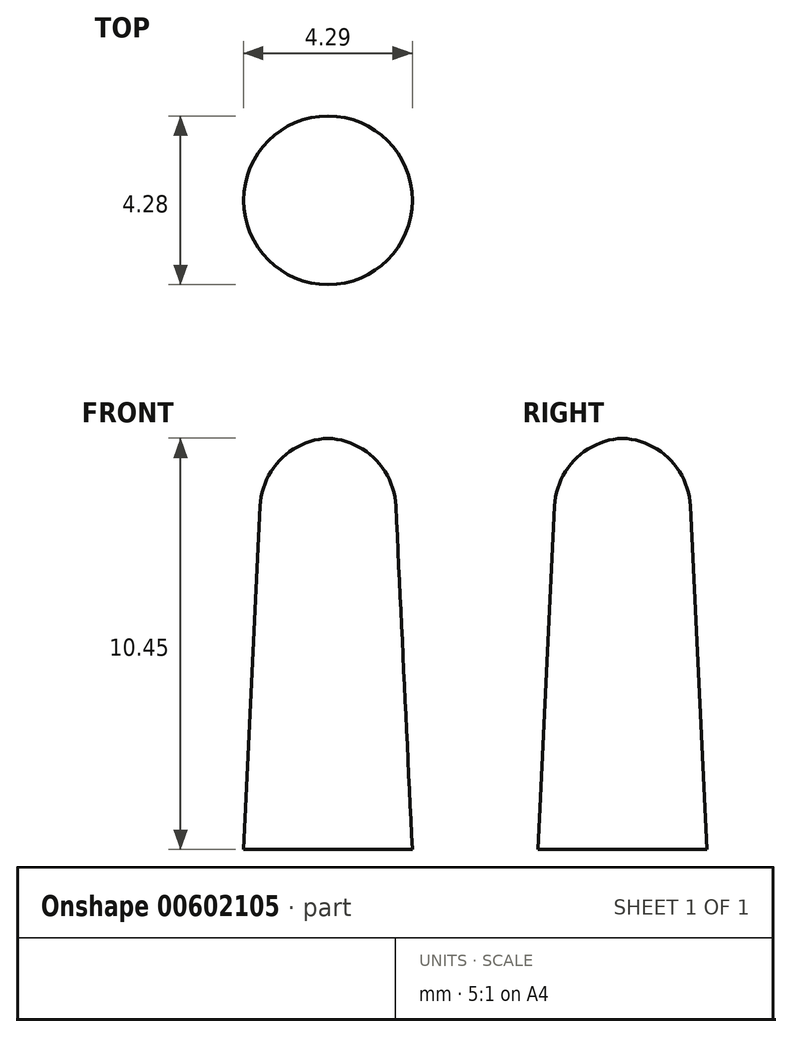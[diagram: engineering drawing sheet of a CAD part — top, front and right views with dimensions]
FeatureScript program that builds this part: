
annotation { "Feature Type Name" : "Feature", "Feature Type Description" : "" }
export const myFeature = defineFeature(function(context is Context, id is Id, definition is map)
    precondition{}
    {
        {
            var Q0;
            Q0=qCreatedBy(makeId("Front.planeOp"),FACE);
            var sketch = newSketch(context, id + "F0", { "sketchPlane" : qUnion([Q0])});
            skLineSegment(sketch, "E0", {"start": v(-32.4, 48.83) * mm, "end": v(-32.4, 38.38) * mm});
            skLineSegment(sketch, "E1", {"start": v(-32.4, 38.38) * mm, "end": v(-30.26, 38.38) * mm});
            skLineSegment(sketch, "E2", {"start": v(-30.68, 47.1) * mm, "end": v(-30.26, 38.38) * mm});
            skArc(sketch, "E3", {"start": v(-30.68, 47.1) * mm, "mid": v(-31.2, 48.3) * mm, "end": v(-32.4, 48.83) * mm});
            skSolve(sketch);
        }
        {
            var Q0;
            Q0=makeQuery(id+"F0.imprint","IMPRINT",FACE,{"disambiguationData":[TD([[makeQuery(id+"F0.imprint","IMPRINT",EDGE,{"derivedFrom":sQuery(id+"F0.wireOp",EDGE,"E0")}),1.0]])]});
            var Q1;
            Q1=sQuery(id+"F0.wireOp",EDGE,"E0");
            revolve(context, id + "F1", {"entities" : qUnion([Q0]), "axis" : qUnion([Q1]), "revolveType" : RevolveType.FULL});
        }
    });
